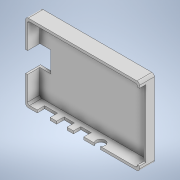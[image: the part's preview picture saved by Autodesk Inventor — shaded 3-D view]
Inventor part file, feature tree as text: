
AUTODESK INVENTOR PART (.ipt)
format: ipt  version: 2020 (Build 240168000, 168)  size: 201,728 bytes
history: native  units: mm
features: sketch x5, extrude x5
ambient origin geometry x8: Origin, YZ Plane, XZ Plane, XY Plane, X Axis, Y Axis, Z Axis, Center Point
bodies: Solid1 (feature_tree)
feature tree (10):
  sketch  "Sketch1"  dims[d0=88.0mm d1=60.0mm]
  extrude  "Extrusion1"  Depth=60.0mm
  extrude  "Extrusion2"  Depth=56.0mm
  sketch  "Sketch2"  dims[d2=85.0mm d3=56.0mm]
  extrude  "Extrusion3"  Depth=3.0mm
  extrude  "Extrusion4"  Depth=2.0mm TaperAngle=0.0deg
  extrude  "Extrusion5"  Depth=4.0mm
  sketch  "Sketch3"  dims[d4=3.0mm d5=3.0mm]
  sketch  "Sketch4"  dims[d6=2.0mm d7=2.0mm d8=0.0mm]
  sketch  "Sketch5"  dims[d9=9.5mm d10=0.0mm d11=4.0mm d12=5.0mm d13=4.0mm d14=53.0mm d15=9.5mm d16=0.0mm d19=7.0mm d22=8.0mm d23=5.0mm d24=8.0mm d25=5.0mm d26=10.0mm d27=32.5mm d28=9.0mm d29=5.8mm d30=9.5mm d31=0.0mm d32=22.0mm d33=22.0mm d34=0.0mm d35=10.0mm d36=15.0mm d37=0.0mm d38=10.5mm]
